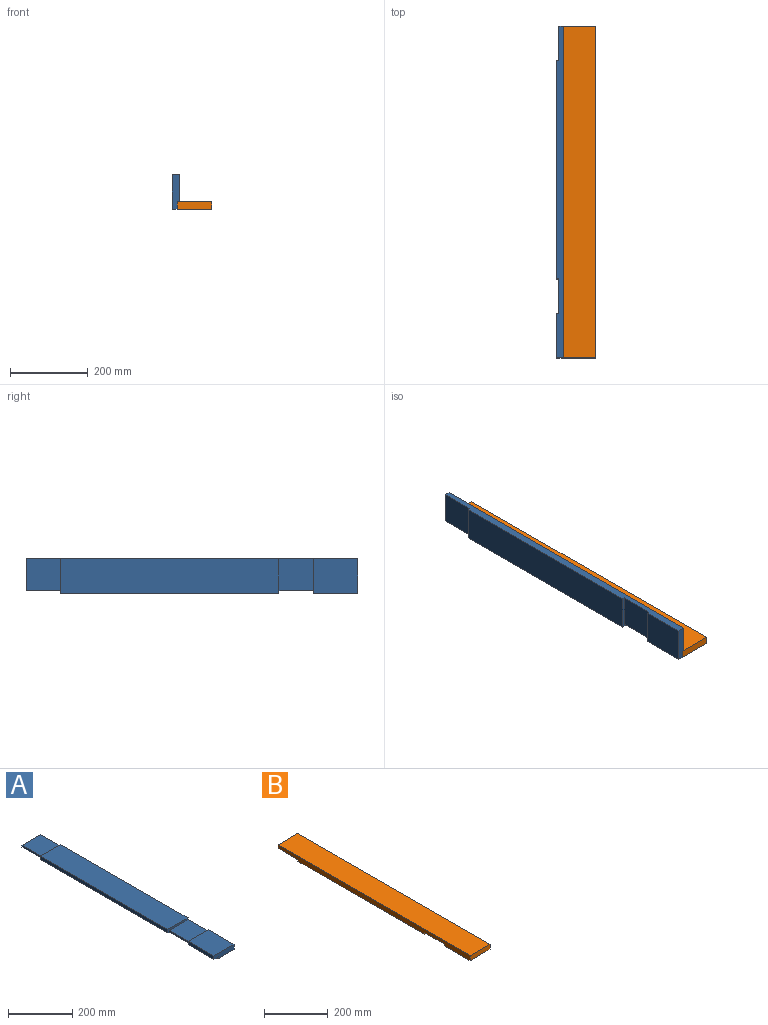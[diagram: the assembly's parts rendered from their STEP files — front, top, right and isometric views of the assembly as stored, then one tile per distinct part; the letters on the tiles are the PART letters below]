
ASSEMBLY  parts=2 mates=1
PART A: 17 faces, bbox 88.9x854.1x19.1 mm
  f0: plane 114.3x12.7mm, normal (-1,0,0), area 1451.6mm2, adj f3,f4,f9,f11
  f1: plane 561.98x12.7mm, normal (-1,0,0), area 7137.1mm2, adj f3,f7,f10,f12
  f2: plane 88.9x82.55mm, normal (0,0,1), area 7338.7mm2, adj f8,f10,f11,f16
  f3: plane 854.08x19.05mm, normal (0,0,-1), area 15141.1mm2, adj f0,f1,f4,f6,f10,f11,f12,f14
  f4: plane 88.9x19.05mm, normal (0,-1,0), area 1572.6mm2, adj f0,f3,f5,f8,f9,f14
  f5: plane 854.08x69.85mm, normal (0,0,-1), area 59657.1mm2, adj f4,f6,f8,f14
  f6: plane 82.55x12.7mm, normal (0,1,0), area 967.7mm2, adj f3,f5,f8,f13,f14,f15
  f7: plane 561.98x88.9mm, normal (0,0,1), area 49959.6mm2, adj f1,f8,f10,f12
  f8: plane 854.08x19.05mm, normal (1,0,0), area 15141.1mm2, adj f2,f4,f5,f6,f7,f9,f10,f11
  f9: plane 114.3x88.9mm, normal (0,0,1), area 10161.3mm2, adj f0,f4,f8,f11
  f10: plane 88.9x12.7mm, normal (0,-1,0), area 604.8mm2, adj f1,f2,f3,f7,f8,f16
  f11: plane 88.9x12.7mm, normal (0,1,0), area 604.8mm2, adj f0,f2,f3,f8,f9,f16
  f12: plane 88.9x12.7mm, normal (0,1,0), area 604.8mm2, adj f1,f3,f7,f8,f13,f15
  f13: plane 88.9x82.55mm, normal (0,0,1), area 7338.7mm2, adj f6,f8,f12,f15
  f14: plane 854.08x6.35mm, normal (-1,0,0), area 5423.4mm2, adj f3,f4,f5,f6
  f15: plane 88.9x6.35mm, normal (-1,0,0), area 564.5mm2, adj f3,f6,f12,f13
  f16: plane 88.9x6.35mm, normal (-1,0,0), area 564.5mm2, adj f2,f3,f10,f11
PART B: 12 faces, bbox 88.9x854.1x19.1 mm
  f0: plane 88.9x12.7mm, normal (0,1,0), area 1129mm2, adj f3,f4,f6,f11
  f1: plane 561.98x88.9mm, normal (0,0,-1), area 49959.6mm2, adj f3,f4,f7,f10
  f2: plane 114.3x88.9mm, normal (0,0,-1), area 10161.3mm2, adj f3,f4,f5,f8
  f3: plane 854.08x19.05mm, normal (-1,0,0), area 15141.1mm2, adj f0,f1,f2,f5,f6,f7,f8,f9
  f4: plane 854.08x19.05mm, normal (1,0,0), area 15141.1mm2, adj f0,f1,f2,f5,f6,f7,f8,f9
  f5: plane 88.9x19.05mm, normal (0,-1,0), area 1693.5mm2, adj f2,f3,f4,f6
  f6: plane 854.08x88.9mm, normal (0,0,1), area 75927.3mm2, adj f0,f3,f4,f5
  f7: plane 88.9x6.35mm, normal (0,-1,0), area 564.5mm2, adj f1,f3,f4,f9
  f8: plane 88.9x6.35mm, normal (0,1,0), area 564.5mm2, adj f2,f3,f4,f9
  f9: plane 88.9x88.9mm, normal (0,0,-1), area 7903.2mm2, adj f3,f4,f7,f8
  f10: plane 88.9x6.35mm, normal (0,1,0), area 564.5mm2, adj f1,f3,f4,f11
  f11: plane 88.9x88.9mm, normal (0,0,-1), area 7903.2mm2, adj f0,f3,f4,f10
PLACE A rot(axis=(0,-1,0),90deg) t=(44.45,0,95.25)mm
PLACE B at identity
MATE fastened A.f3 <-> B.f3  axis (1,0,0) through (38.1,0,0)mm
